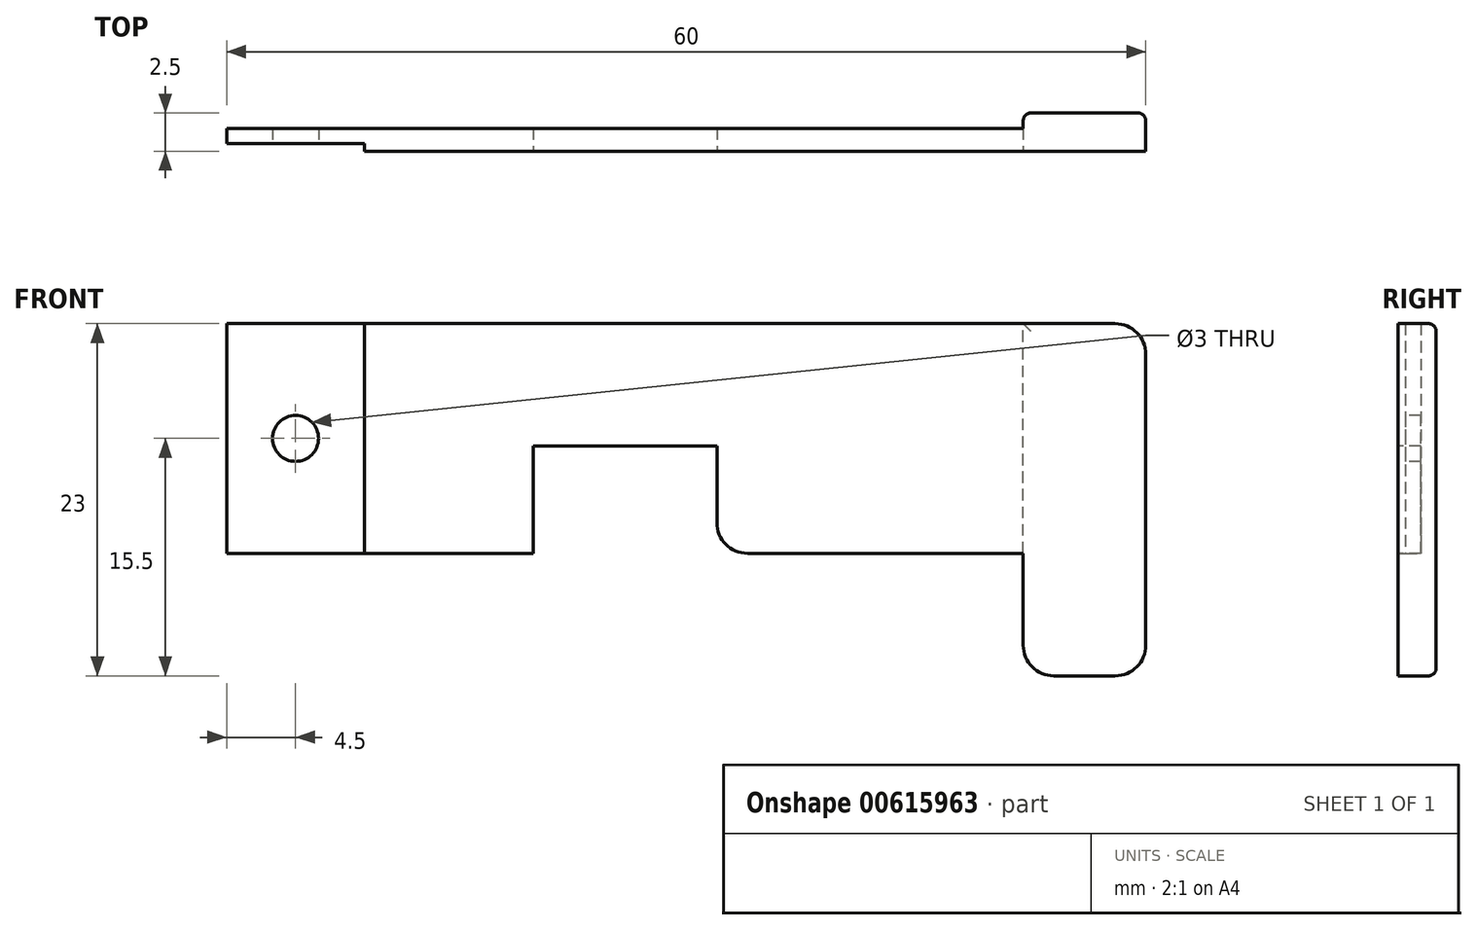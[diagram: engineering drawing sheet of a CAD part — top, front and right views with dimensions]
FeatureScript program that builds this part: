
annotation { "Feature Type Name" : "Feature", "Feature Type Description" : "" }
export const myFeature = defineFeature(function(context is Context, id is Id, definition is map)
    precondition{}
    {
        {
            var Q0;
            Q0=qCreatedBy(makeId("Front.planeOp"),FACE);
            var sketch = newSketch(context, id + "F0", { "sketchPlane" : qUnion([Q0])});
            skLineSegment(sketch, "E0.bottom", {"start": v(-37, 7.5) * mm, "end": v(25, 7.5) * mm});
            skLineSegment(sketch, "E0.top", {"start": v(-37, -7.5) * mm, "end": v(25, -7.5) * mm});
            skLineSegment(sketch, "E0.left", {"start": v(-37, 7.5) * mm, "end": v(-37, -7.5) * mm});
            skLineSegment(sketch, "E0.right", {"start": v(25, 7.5) * mm, "end": v(25, -7.5) * mm});
            skPoint(sketch, "E0.middle", {"position": v(-6, 0) * mm});
            skSolve(sketch);
        }
        {
            var Q0;
            Q0 = qSketchRegion(id + "F0", true);
            extrude(context, id + "F1", {"entities" : qUnion([Q0]), "depth" : 1.5 * mm, "offsetDistance" : 25 * mm});
        }
        {
            var Q0;
            Q0=makeQuery(id+"F1.opExtrude","CAP_FACE",FACE,{"disambiguationData":[OSD([sQuery(id+"F0.wireOp",EDGE,"E0.bottom"),sQuery(id+"F0.wireOp",EDGE,"E0.top"),sQuery(id+"F0.wireOp",EDGE,"E0.left"),sQuery(id+"F0.wireOp",EDGE,"E0.right")])],"isStart":false});
            var sketch = newSketch(context, id + "F2", { "sketchPlane" : qUnion([Q0])});
            skLineSegment(sketch, "E1.bottom", {"start": v(25, -7.5) * mm, "end": v(15, -7.5) * mm});
            skLineSegment(sketch, "E1.top", {"start": v(25, -15.5) * mm, "end": v(15, -15.5) * mm});
            skLineSegment(sketch, "E1.left", {"start": v(25, -7.5) * mm, "end": v(25, -15.5) * mm});
            skLineSegment(sketch, "E1.right", {"start": v(15, -7.5) * mm, "end": v(15, -15.5) * mm});
            skSolve(sketch);
        }
        {
            var Q0;
            Q0 = qSketchRegion(id + "F2", true);
            var Q1;
            Q1=makeQuery(id+"F1.opExtrude","CAP_FACE",FACE,{"disambiguationData":[OSD([sQuery(id+"F0.wireOp",EDGE,"E0.bottom"),sQuery(id+"F0.wireOp",EDGE,"E0.top"),sQuery(id+"F0.wireOp",EDGE,"E0.left"),sQuery(id+"F0.wireOp",EDGE,"E0.right")])],"isStart":true});
            extrude(context, id + "F3", {"entities" : qUnion([Q0]), "operationType" : NewBodyOperationType.ADD, "endBound" : BoundingType.UP_TO_SURFACE, "oppositeDirection" : true, "depth" : 25 * mm, "endBoundEntityFace" : qUnion([Q1]), "offsetDistance" : 25 * mm});
        }
        {
            var Q0;
            Q0=makeQuery(id+"F3.boolean.opBoolean","MERGE",FACE,{"derivedFrom":[makeQuery(id+"F1.opExtrude","CAP_FACE",FACE,{"disambiguationData":[OSD([sQuery(id+"F0.wireOp",EDGE,"E0.bottom"),sQuery(id+"F0.wireOp",EDGE,"E0.top"),sQuery(id+"F0.wireOp",EDGE,"E0.left"),sQuery(id+"F0.wireOp",EDGE,"E0.right")])],"isStart":false}),makeQuery(id+"F3.opExtrude","CAP_FACE",FACE,{"disambiguationData":[OSD([sQuery(id+"F2.wireOp",EDGE,"E1.bottom"),sQuery(id+"F2.wireOp",EDGE,"E1.top"),sQuery(id+"F2.wireOp",EDGE,"E1.left"),sQuery(id+"F2.wireOp",EDGE,"E1.right")])],"isStart":true})]});
            var sketch = newSketch(context, id + "F4", { "sketchPlane" : qUnion([Q0])});
            skLineSegment(sketch, "E2.bottom", {"start": v(-17, -7.5) * mm, "end": v(-5, -7.5) * mm});
            skLineSegment(sketch, "E2.top", {"start": v(-17, -0.5) * mm, "end": v(-5, -0.5) * mm});
            skLineSegment(sketch, "E2.left", {"start": v(-17, -7.5) * mm, "end": v(-17, -0.5) * mm});
            skLineSegment(sketch, "E2.right", {"start": v(-5, -7.5) * mm, "end": v(-5, -0.5) * mm});
            skSolve(sketch);
        }
        {
            var Q0;
            Q0 = qSketchRegion(id + "F4", true);
            extrude(context, id + "F5", {"entities" : qUnion([Q0]), "operationType" : NewBodyOperationType.REMOVE, "endBound" : BoundingType.THROUGH_ALL, "oppositeDirection" : true, "depth" : 25 * mm, "offsetDistance" : 25 * mm});
        }
        {
            var Q0;
            Q0=makeQuery(id+"F3.boolean.opBoolean","MERGE",FACE,{"derivedFrom":[makeQuery(id+"F1.opExtrude","CAP_FACE",FACE,{"disambiguationData":[OSD([sQuery(id+"F0.wireOp",EDGE,"E0.bottom"),sQuery(id+"F0.wireOp",EDGE,"E0.top"),sQuery(id+"F0.wireOp",EDGE,"E0.left"),sQuery(id+"F0.wireOp",EDGE,"E0.right")])],"isStart":false}),makeQuery(id+"F3.opExtrude","CAP_FACE",FACE,{"disambiguationData":[OSD([sQuery(id+"F2.wireOp",EDGE,"E1.bottom"),sQuery(id+"F2.wireOp",EDGE,"E1.top"),sQuery(id+"F2.wireOp",EDGE,"E1.left"),sQuery(id+"F2.wireOp",EDGE,"E1.right")])],"isStart":true})]});
            var sketch = newSketch(context, id + "F6", { "sketchPlane" : qUnion([Q0])});
            skCircle(sketch, "E3", {"center": v(-32.5, 0) * mm, "radius": 1.5 * mm});
            skSolve(sketch);
        }
        {
            var Q0;
            Q0 = qSketchRegion(id + "F6", true);
            extrude(context, id + "F7", {"entities" : qUnion([Q0]), "operationType" : NewBodyOperationType.REMOVE, "endBound" : BoundingType.THROUGH_ALL, "oppositeDirection" : true, "depth" : 25 * mm, "offsetDistance" : 25 * mm});
        }
        {
            var Q0;
            {var subQ1=sQuery(id+"F0.wireOp",EDGE,"E0.left");var subQ2=sQuery(id+"F0.wireOp",EDGE,"E0.top");Q0=makeQuery(id+"F5.boolean.opBoolean","SPLIT",FACE,{"disambiguationData":[TD([makeQuery(id+"F1.opExtrude","SWEPT_FACE",FACE,{"disambiguationData":[OSD([subQ1])]})])],"derivedFrom":makeQuery(id+"F1.opExtrude","SWEPT_FACE",FACE,{"disambiguationData":[OSD([subQ2])]})});}
            var sketch = newSketch(context, id + "F8", { "sketchPlane" : qUnion([Q0])});
            skPoint(sketch, "E4.oppositeSnap0", {"position": v(-37, 1) * mm});
            skLineSegment(sketch, "E4.bottom", {"start": v(-37, 1.5) * mm, "end": v(-28, 1.5) * mm});
            skLineSegment(sketch, "E4.top", {"start": v(-37, 1) * mm, "end": v(-28, 1) * mm});
            skLineSegment(sketch, "E4.left", {"start": v(-37, 1.5) * mm, "end": v(-37, 1) * mm});
            skLineSegment(sketch, "E4.right", {"start": v(-28, 1.5) * mm, "end": v(-28, 1) * mm});
            skSolve(sketch);
        }
        {
            var Q0;
            Q0 = qSketchRegion(id + "F8", true);
            extrude(context, id + "F9", {"entities" : qUnion([Q0]), "operationType" : NewBodyOperationType.REMOVE, "endBound" : BoundingType.THROUGH_ALL, "oppositeDirection" : true, "depth" : 25 * mm, "offsetDistance" : 25 * mm});
        }
        {
            var Q0;
            Q0=makeQuery(id+"F3.opExtrude","SWEPT_FACE",FACE,{"disambiguationData":[OSD([sQuery(id+"F2.wireOp",EDGE,"E1.top")])]});
            var sketch = newSketch(context, id + "F10", { "sketchPlane" : qUnion([Q0])});
            skLineSegment(sketch, "E5.bottom", {"start": v(25, 1.5) * mm, "end": v(23, 1.5) * mm});
            skLineSegment(sketch, "E5.top", {"start": v(25, 0) * mm, "end": v(23, 0) * mm});
            skLineSegment(sketch, "E5.left", {"start": v(25, 1.5) * mm, "end": v(25, 0) * mm});
            skLineSegment(sketch, "E5.right", {"start": v(23, 1.5) * mm, "end": v(23, 0) * mm});
            skSolve(sketch);
        }
        {
            var Q0;
            Q0 = qSketchRegion(id + "F10", true);
            extrude(context, id + "F11", {"entities" : qUnion([Q0]), "operationType" : NewBodyOperationType.REMOVE, "endBound" : BoundingType.THROUGH_ALL, "oppositeDirection" : true, "depth" : 25 * mm, "offsetDistance" : 25 * mm});
        }
        {
            var Q0;
            {var subQ0=sQuery(id+"F0.wireOp",EDGE,"E0.right");var subQ1=sQuery(id+"F0.wireOp",EDGE,"E0.left");var subQ2=sQuery(id+"F0.wireOp",EDGE,"E0.top");var subQ3=sQuery(id+"F0.wireOp",EDGE,"E0.bottom");Q0=makeQuery(id+"F3.boolean.opBoolean","MERGE",FACE,{"derivedFrom":[makeQuery(id+"F1.opExtrude","CAP_FACE",FACE,{"disambiguationData":[OSD([subQ3,subQ2,subQ1,subQ0])],"isStart":true}),makeQuery(id+"F3.opExtrude","CAP_FACE",FACE,{"disambiguationData":[OSD([subQ3,subQ2,subQ1,subQ0])],"isStart":false})]});}
            var sketch = newSketch(context, id + "F12", { "sketchPlane" : qUnion([Q0])});
            skPoint(sketch, "E6.oppositeSnap0", {"position": v(-15, -11.5) * mm});
            skLineSegment(sketch, "E6.bottom", {"start": v(-23, -15.5) * mm, "end": v(-15, -15.5) * mm});
            skLineSegment(sketch, "E6.top", {"start": v(-23, 7.5) * mm, "end": v(-15, 7.5) * mm});
            skLineSegment(sketch, "E6.left", {"start": v(-23, -15.5) * mm, "end": v(-23, 7.5) * mm});
            skLineSegment(sketch, "E6.right", {"start": v(-15, -15.5) * mm, "end": v(-15, 7.5) * mm});
            skSolve(sketch);
        }
        {
            var Q0;
            Q0 = qSketchRegion(id + "F12", true);
            extrude(context, id + "F13", {"entities" : qUnion([Q0]), "operationType" : NewBodyOperationType.ADD, "depth" : 1 * mm, "offsetDistance" : 25 * mm});
        }
        {
            var Q0;
            Q0=makeQuery(id+"F13.boolean.opBoolean","MERGE",EDGE,{"derivedFrom":[makeQuery(id+"F3.opExtrude","SWEPT_EDGE",EDGE,{"disambiguationData":[OSD([sQuery(id+"F2.wireOp",EDGE,"E1.top"),sQuery(id+"F2.wireOp",EDGE,"E1.right")])]}),makeQuery(id+"F13.opExtrude","SWEPT_EDGE",EDGE,{"disambiguationData":[OSD([sQuery(id+"F12.wireOp",EDGE,"E6.bottom"),sQuery(id+"F12.wireOp",EDGE,"E6.right")])]})]});
            var Q1;
            Q1=makeQuery(id+"F13.boolean.opBoolean","MERGE",EDGE,{"derivedFrom":[makeQuery(id+"F11.boolean.opBoolean","COPY",EDGE,{"derivedFrom":makeQuery(id+"F11.opExtrude","CAP_EDGE",EDGE,{"disambiguationData":[OSD([sQuery(id+"F10.wireOp",EDGE,"E5.right")])],"isStart":true})}),makeQuery(id+"F13.opExtrude","SWEPT_EDGE",EDGE,{"disambiguationData":[OSD([sQuery(id+"F12.wireOp",EDGE,"E6.bottom"),sQuery(id+"F12.wireOp",EDGE,"E6.left")])]})]});
            var Q2;
            Q2=makeQuery(id+"F13.boolean.opBoolean","MERGE",EDGE,{"derivedFrom":[makeQuery(id+"F11.boolean.opBoolean","INTERSECT",EDGE,{"derivedFrom":[makeQuery(id+"F1.opExtrude","SWEPT_FACE",FACE,{"disambiguationData":[OSD([sQuery(id+"F0.wireOp",EDGE,"E0.bottom")])]}),makeQuery(id+"F11.opExtrude","SWEPT_FACE",FACE,{"disambiguationData":[OSD([sQuery(id+"F10.wireOp",EDGE,"E5.right")])]})]}),makeQuery(id+"F13.opExtrude","SWEPT_EDGE",EDGE,{"disambiguationData":[OSD([sQuery(id+"F12.wireOp",EDGE,"E6.top"),sQuery(id+"F12.wireOp",EDGE,"E6.left")])]})]});
            var Q3;
            Q3=makeQuery(id+"F5.boolean.opBoolean","COPY",EDGE,{"derivedFrom":makeQuery(id+"F5.opExtrude","SWEPT_EDGE",EDGE,{"disambiguationData":[OSD([sQuery(id+"F0.wireOp",EDGE,"E0.top"),sQuery(id+"F4.wireOp",EDGE,"E2.bottom"),sQuery(id+"F4.wireOp",EDGE,"E2.right")])]})});
            var Q4;
            Q4=makeQuery(id+"F5.boolean.opBoolean","COPY",EDGE,{"derivedFrom":makeQuery(id+"F5.opExtrude","SWEPT_EDGE",EDGE,{"disambiguationData":[OSD([sQuery(id+"F0.wireOp",EDGE,"E0.top"),sQuery(id+"F4.wireOp",EDGE,"E2.bottom"),sQuery(id+"F4.wireOp",EDGE,"E2.left")])]})});
            fillet(context, id + "F14", {"entities" : qUnion([Q0, Q1, Q2, Q3, Q4]), "radius" : 2 * mm, "tangentPropagation" : true, "allowEdgeOverflow" : false});
        }
        {
            var Q0;
            Q0=makeQuery(id+"F13.opExtrude","CAP_EDGE",EDGE,{"disambiguationData":[OSD([sQuery(id+"F12.wireOp",EDGE,"E6.left")])],"isStart":false});
            var Q1;
            Q1=makeQuery(id+"F11.boolean.opBoolean","COPY",EDGE,{"derivedFrom":makeQuery(id+"F11.opExtrude","SWEPT_EDGE",EDGE,{"disambiguationData":[OSD([sQuery(id+"F2.wireOp",EDGE,"E1.top"),sQuery(id+"F10.wireOp",EDGE,"E5.bottom"),sQuery(id+"F10.wireOp",EDGE,"E5.right")])]})});
            fillet(context, id + "F15", {"entities" : qUnion([Q0, Q1]), "radius" : 0.5 * mm, "tangentPropagation" : true, "allowEdgeOverflow" : false});
        }
    });
